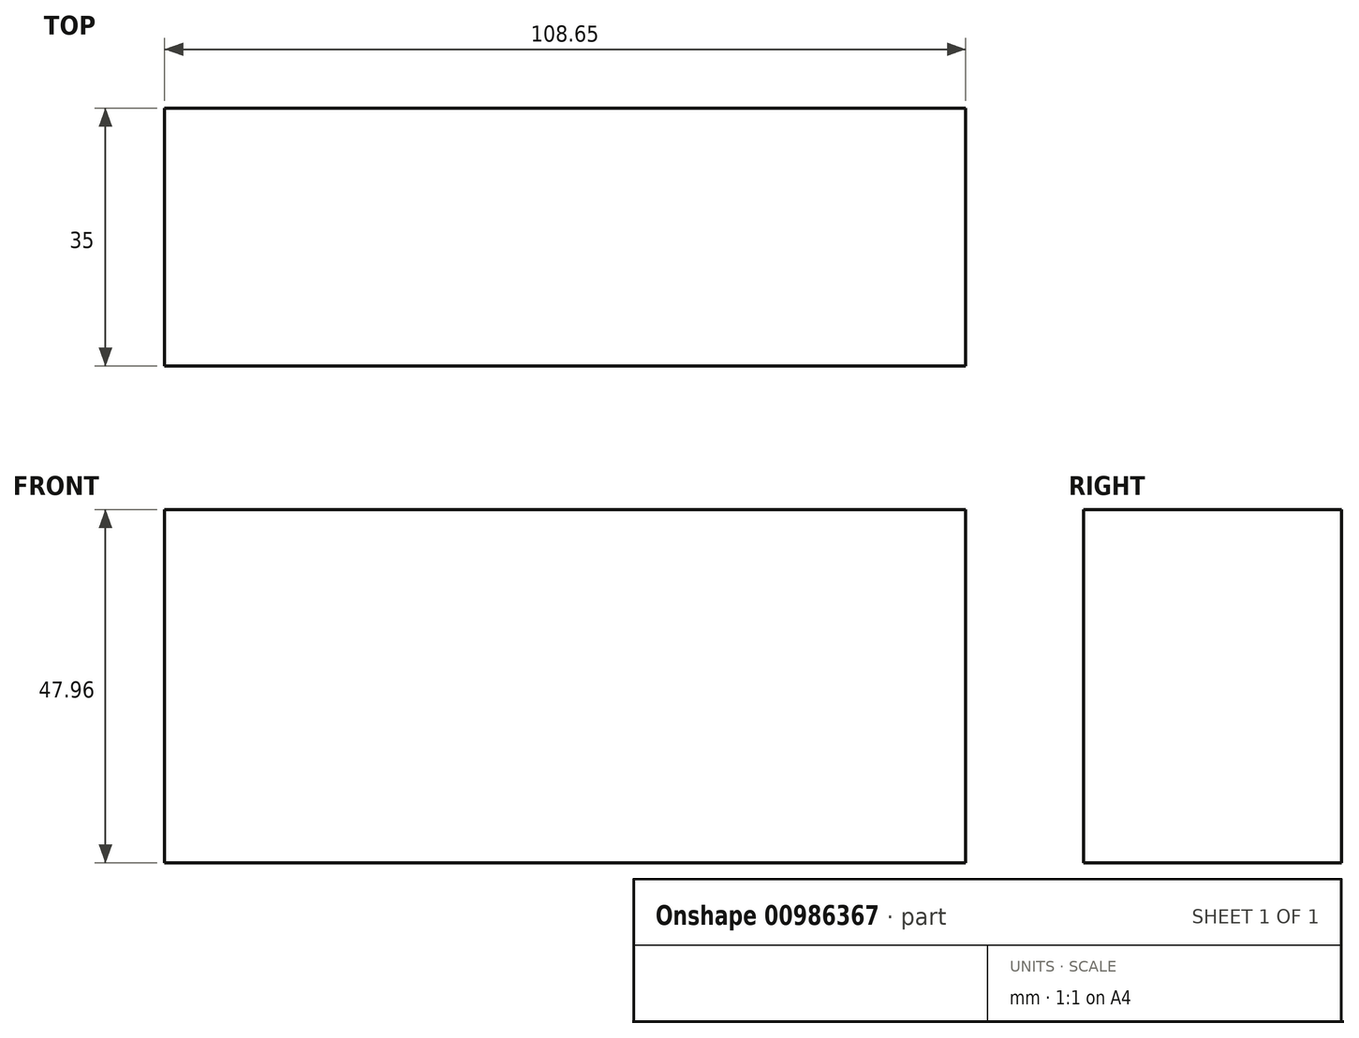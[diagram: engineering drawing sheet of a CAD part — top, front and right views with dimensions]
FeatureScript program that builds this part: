
annotation { "Feature Type Name" : "Feature", "Feature Type Description" : "" }
export const myFeature = defineFeature(function(context is Context, id is Id, definition is map)
    precondition{}
    {
        {
            var Q0;
            Q0=qCreatedBy(makeId("Front.planeOp"),FACE);
            var sketch = newSketch(context, id + "F0", { "sketchPlane" : qUnion([Q0])});
            skLineSegment(sketch, "E0.bottom", {"start": v(-47.22, -22.94) * mm, "end": v(61.43, -22.94) * mm});
            skLineSegment(sketch, "E0.top", {"start": v(-47.22, 25.02) * mm, "end": v(61.43, 25.02) * mm});
            skLineSegment(sketch, "E0.left", {"start": v(-47.22, -22.94) * mm, "end": v(-47.22, 25.02) * mm});
            skLineSegment(sketch, "E0.right", {"start": v(61.43, -22.94) * mm, "end": v(61.43, 25.02) * mm});
            skSolve(sketch);
        }
        {
            var Q0;
            Q0=makeQuery(id+"F0.imprint","IMPRINT",FACE,{"disambiguationData":[TD([[makeQuery(id+"F0.imprint","IMPRINT",EDGE,{"derivedFrom":sQuery(id+"F0.wireOp",EDGE,"E0.bottom")}),1.0]])]});
            extrude(context, id + "F1", {"entities" : qUnion([Q0]), "oppositeDirection" : true, "depth" : 25 * mm, "offsetDistance" : 25 * mm, "hasSecondDirection" : true, "secondDirectionOppositeDirection" : false, "secondDirectionDepth" : 10 * mm});
        }
    });
